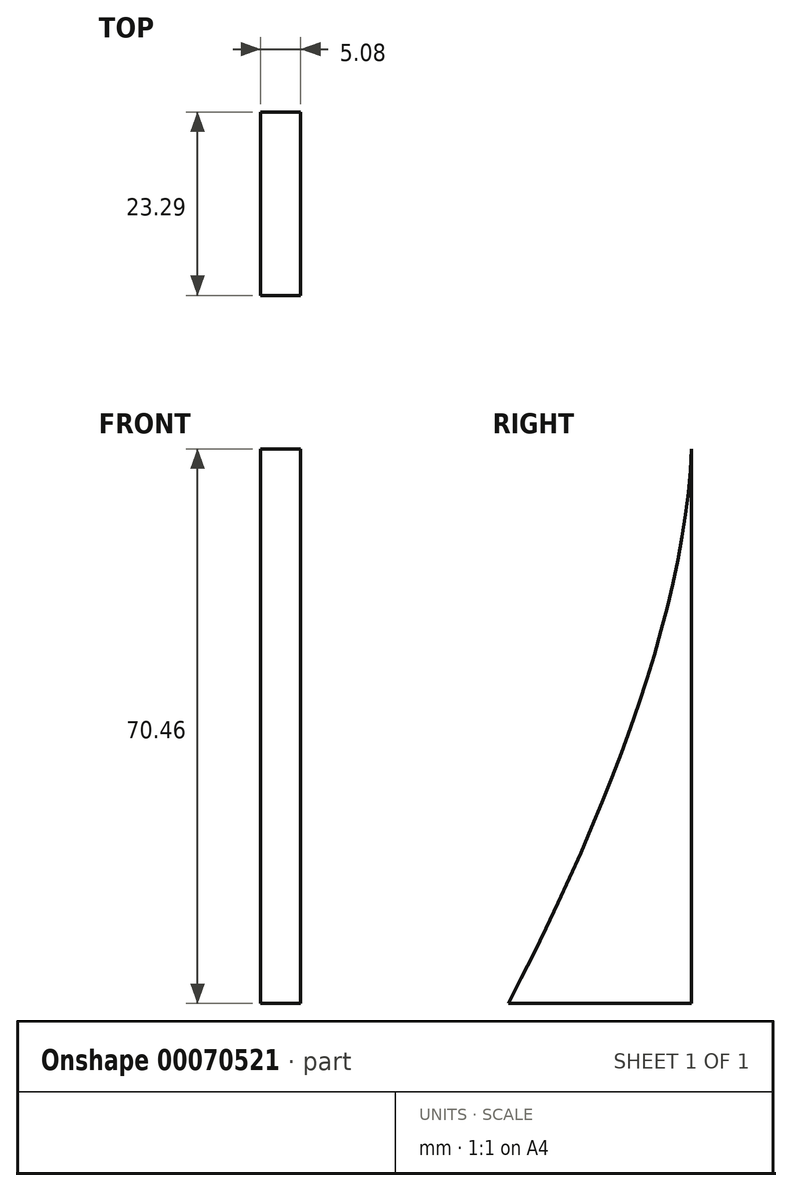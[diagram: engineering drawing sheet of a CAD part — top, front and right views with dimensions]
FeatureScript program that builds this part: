
annotation { "Feature Type Name" : "Feature", "Feature Type Description" : "" }
export const myFeature = defineFeature(function(context is Context, id is Id, definition is map)
    precondition{}
    {
        {
            var Q0;
            Q0=qCreatedBy(makeId("Right.planeOp"),FACE);
            var sketch = newSketch(context, id + "F0", { "sketchPlane" : qUnion([Q0])});
            skLineSegment(sketch, "E0.bottom", {"start": v(-194.54, 77.91) * mm, "end": v(421.15, 77.91) * mm});
            skLineSegment(sketch, "E0.top", {"start": v(-194.54, -74.49) * mm, "end": v(618.26, -74.49) * mm});
            skLineSegment(sketch, "E0.left", {"start": v(-194.54, 77.91) * mm, "end": v(-194.54, -74.49) * mm});
            skLineSegment(sketch, "E0.right", {"start": v(618.26, 1.71) * mm, "end": v(618.26, -74.49) * mm});
            skFitSpline(sketch, "E1", {"points": [v(302.48, 77.91) * mm, v(618.26, 1.71) * mm, v(531.74, -164.98) * mm, v(531.74, -162.84) * mm, v(530.66, -162.84) * mm], "startDerivative": vector(889.52, 10.4) * mm, "endDerivative": vector(-47.3, -16.45) * mm});
            skPoint(sketch, "E2.orphan", {"position": v(618.26, 77.91) * mm});
            skSolve(sketch);
        }
        {
            var Q0;
            {var subQ1=sQuery(id+"F0.wireOp",EDGE,"E0.top");Q0=makeQuery(id+"F0.imprint","IMPRINT",FACE,{"disambiguationData":[TD([[makeQuery(id+"F0.imprint","IMPRINT",EDGE,{"derivedFrom":subQ1}),1.0]])]});}
            extrude(context, id + "F1", {"entities" : qUnion([Q0]), "depth" : 5.08 * mm});
        }
    });
